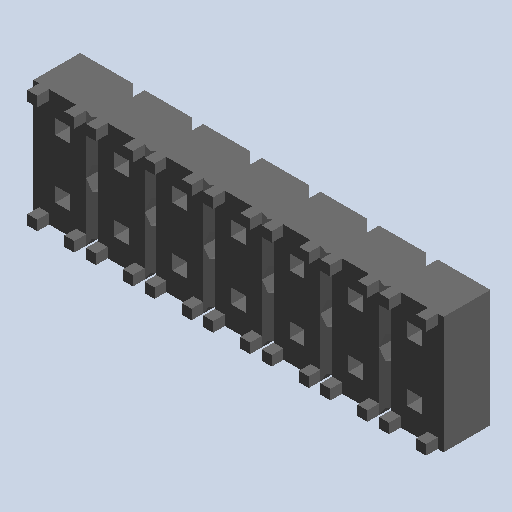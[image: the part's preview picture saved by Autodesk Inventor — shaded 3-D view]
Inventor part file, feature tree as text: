
AUTODESK INVENTOR PART (.ipt)
format: ipt  version: 2024.2 (Build 282272000, 272)  size: 454,656 bytes
history: native  units: mm (DEFAULTED — no unit token found)
features: extrude x9, sketch x9, other x7, pattern_linear x1
ambient origin geometry x8: Origin, YZ Plane, XZ Plane, XY Plane, X Axis, Y Axis, Z Axis, Center Point
bodies: Solid1 (feature_tree), body_XY (feature_tree), body_YZ (feature_tree), body_ZX (feature_tree), body_X (feature_tree), body_Y (feature_tree), body_Z (feature_tree), body_Center (feature_tree)
feature tree (26):
  extrude  "Extrusion1"  Depth=2.54mm TaperAngle=0.0deg
  extrude  "Extrusion2"  Depth=10.16mm TaperAngle=0.0deg
  extrude  "Extrusion3"  Depth=10.16mm TaperAngle=0.0deg
  extrude  "Extrusion4"  Depth=10.16mm TaperAngle=0.0deg
  extrude  "Extrusion5"  Depth=2.54mm TaperAngle=0.0deg
  extrude  "Extrusion6"  [1 undecoded]
  extrude  "Extrusion7"  [1 undecoded]
  extrude  "Extrusion8"  [1 undecoded]
  extrude  "Extrusion9"  [1 undecoded]
  pattern_linear  "Rectangular Pattern1"  [2 undecoded]
  other  "pin_XY"
  other  "pin_YZ"
  other  "pin_ZX"
  other  "pin_X"
  other  "pin_Y"
  other  "pin_Z"
  other  "pin_Center"
  sketch  "Sketch_1"  dims[d0=2.54mm d1=0.0mm d2=35.56mm d3=0.0mm]
  sketch  "Sketch_2"  dims[d4=35.56mm d5=0.0mm d6=10.16mm d7=0.0mm]
  sketch  "Sketch_3"  dims[d8=10.16mm d9=0.0mm d10=35.56mm d11=0.0mm]
  sketch  "Sketch_6"  dims[d12=10.16mm d13=0.0mm d14=10.16mm d15=0.0mm]
  sketch  "Sketch_9"  dims[d16=5.08mm d17=0.0mm d18=60.0mm d20=2.54mm d21=10.0mm d23=0.0mm]
  sketch  "Sketch_11"
  sketch  "Sketch_18"
  sketch  "Sketch_20"
  sketch  "Sketch_17"
note: 6 required parameter values undecoded (feature->parameter linkage not recoverable at this tier; creation-order binding heuristic only, values carry confidence <= 0.55)
